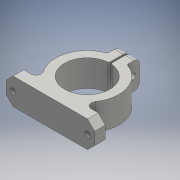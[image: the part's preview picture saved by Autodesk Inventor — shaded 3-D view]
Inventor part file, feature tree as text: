
AUTODESK INVENTOR PART (.ipt)
format: ipt  version: 2016 (Build 200138000, 138)  size: 168,448 bytes
history: native  units: mm
features: sketch x3, extrude x2, chamfer x1, hole x1, fillet x1, mirror x1
ambient origin geometry x8: Origin, YZ Plane, XZ Plane, XY Plane, X Axis, Y Axis, Z Axis, Center Point
bodies: Solid1 (feature_tree)
feature tree (9):
  extrude  "Extrusion1"  Depth=5.0mm
  extrude  "Extrusion2"  Depth=6.0mm
  chamfer  "Chamfer1"  Distance=3.0mm
  hole  "Hole1"  [1 undecoded]
  fillet  "Fillet1"  Radius=5.0mm
  mirror  "Mirror1"
  sketch  "Sketch1"  dims[d0=12.8mm d2=5.0mm]
  sketch  "Sketch2"  dims[d3=25.0mm d4=6.0mm]
  sketch  "Sketch3"  dims[d5=8.0mm d6=3.0mm d7=1.0mm d8=5.0mm d9=7.0mm d10=15.0mm d11=0.0mm d12=4.0mm d13=2.0mm d14=45.0deg d15=3.2mm d16=15.0mm d17=0.0mm d19=3.2mm d20=6.0mm d21=4.0mm d22=2.0mm d23=90.0deg d24=8.0mm d25=20.594885mm d26=3.0mm d27=1.0mm]
note: 1 required parameter value undecoded (feature->parameter linkage not recoverable at this tier; creation-order binding heuristic only, values carry confidence <= 0.55)
